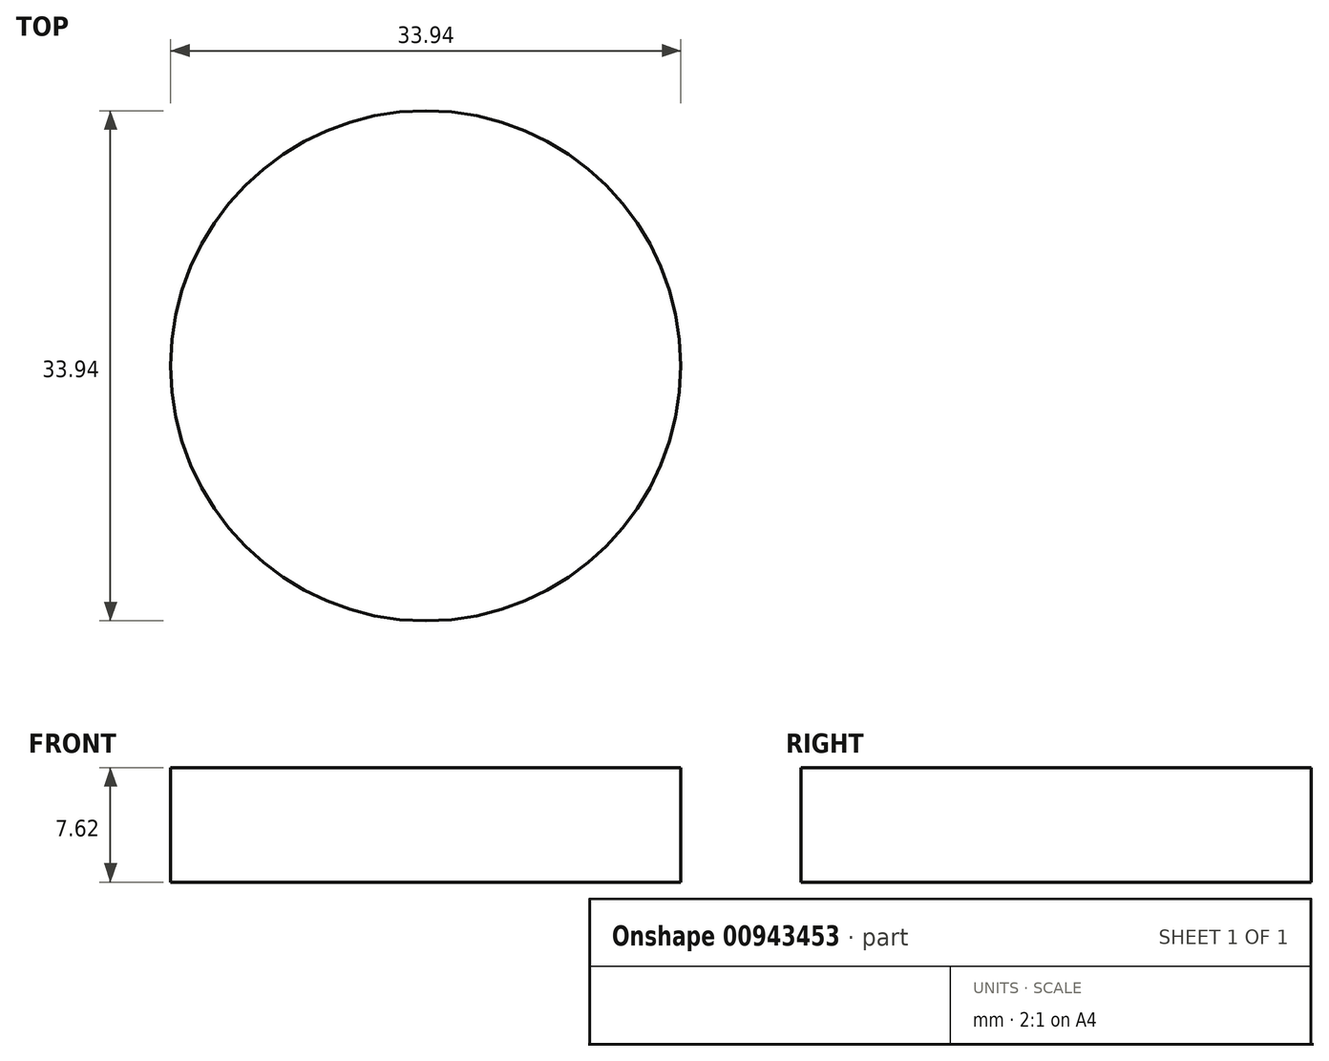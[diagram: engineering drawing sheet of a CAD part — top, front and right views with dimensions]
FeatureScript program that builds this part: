
annotation { "Feature Type Name" : "Feature", "Feature Type Description" : "" }
export const myFeature = defineFeature(function(context is Context, id is Id, definition is map)
    precondition{}
    {
        {
            var Q0;
            Q0=qCreatedBy(makeId("Top.planeOp"),FACE);
            var sketch = newSketch(context, id + "F0", { "sketchPlane" : qUnion([Q0])});
            skCircle(sketch, "E0", {"center": v(-45.74, 32.98) * mm, "radius": 25.94 * mm});
            skLineSegment(sketch, "E1", {"start": v(13.52, 57.2) * mm, "end": v(13.52, 15.46) * mm});
            skSolve(sketch);
        }
        {
            var Q0;
            Q0=qCreatedBy(makeId("Top.planeOp"),FACE);
            var sketch = newSketch(context, id + "F1", { "sketchPlane" : qUnion([Q0])});
            skCircle(sketch, "E2", {"center": v(-45.82, 33.25) * mm, "radius": 16.97 * mm});
            skCircle(sketch, "E3", {"center": v(-45.82, 33.38) * mm, "radius": 11.62 * mm});
            skSolve(sketch);
        }
        {
            var Q0;
            Q0=makeQuery(id+"F1.imprint","IMPRINT",FACE,{"disambiguationData":[TD([[makeQuery(id+"F1.imprint","IMPRINT",EDGE,{"derivedFrom":sQuery(id+"F1.wireOp",EDGE,"E2")}),1.0]])]});
            var Q1;
            Q1=makeQuery(id+"F1.imprint","IMPRINT",FACE,{"disambiguationData":[TD([[makeQuery(id+"F1.imprint","IMPRINT",EDGE,{"derivedFrom":sQuery(id+"F1.wireOp",EDGE,"E3")}),1.0]])]});
            extrude(context, id + "F2", {"entities" : qUnion([Q0, Q1]), "depth" : 7.62 * mm, "offsetDistance" : 25.4 * mm});
        }
    });
